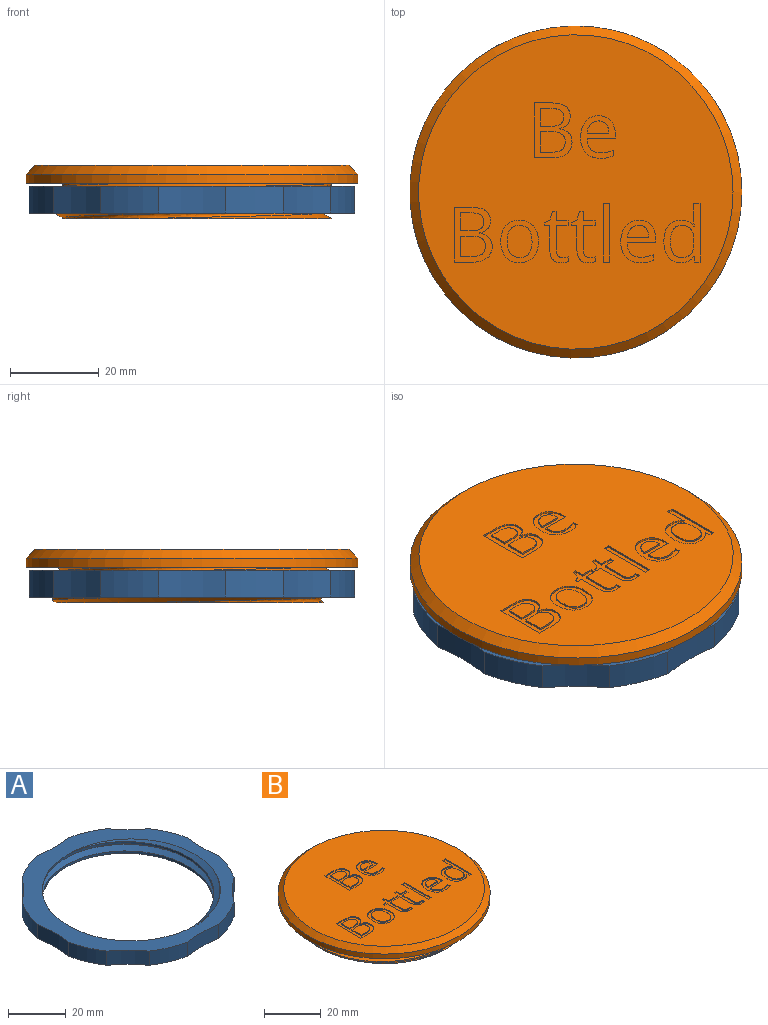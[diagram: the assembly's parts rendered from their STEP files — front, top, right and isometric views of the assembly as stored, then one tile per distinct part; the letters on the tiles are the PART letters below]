
ASSEMBLY  parts=2 mates=1
PART A: 22 faces, bbox 74.7x75.4x10.5 mm
  f0: plane 74.73x74.73mm, normal (0,0,-1), area 1345.5mm2, adj f1,f2,f3,f4,f5,f6,f7,f9
  f1: cylinder r=37.5mm len=13.18mm, axis (0,0,-1), area 86.1mm2, adj f0,f8,f14,f21
  f2: cylinder r=37.5mm len=13.18mm, axis (0,0,-1), area 86.1mm2, adj f0,f8,f20,f21
  f3: cylinder r=37.5mm len=13.18mm, axis (0,0,-1), area 86.1mm2, adj f0,f8,f19,f20
  f4: cylinder r=37.5mm len=13.18mm, axis (0,0,-1), area 86.1mm2, adj f0,f8,f18,f19
  f5: cylinder r=37.5mm len=13.18mm, axis (0,0,-1), area 86.1mm2, adj f0,f8,f17,f18
  f6: cylinder r=37.5mm len=13.18mm, axis (0,0,-1), area 86.1mm2, adj f0,f8,f16,f17
  f7: cylinder r=37.5mm len=13.18mm, axis (0,0,-1), area 86.1mm2, adj f0,f8,f15,f16
  f8: plane 74.73x74.73mm, normal (0,0,1), area 1345.4mm2, adj f1,f2,f3,f4,f5,f6,f7,f9
  f9: cylinder r=37.5mm len=13.18mm, axis (0,0,-1), area 86.1mm2, adj f0,f8,f14,f15
  f10: bspline ~73.7x63.83mm, area 726.9mm2, adj f0,f8,f12,f13
  f11: bspline ~73.7x63.83mm, area 726.7mm2, adj f0,f8,f12,f13
  f12: bspline ~74.12x64.19mm, area 174.8mm2, adj f0,f8,f10,f11
  f13: cylinder r=29.75mm len=59.5mm, axis (0,0,-1), area 280.5mm2, adj f0,f8,f10,f11
  f14: cylinder r=48.3mm len=10.61mm, axis (0,0,-1), area 90.4mm2, adj f0,f1,f8,f9
  f15: cylinder r=48.3mm len=15mm, axis (0,0,-1), area 90.4mm2, adj f0,f7,f8,f9
  f16: cylinder r=48.3mm len=10.61mm, axis (0,0,-1), area 90.4mm2, adj f0,f6,f7,f8
  f17: cylinder r=48.3mm len=15mm, axis (0,0,-1), area 90.4mm2, adj f0,f5,f6,f8
  f18: cylinder r=48.3mm len=10.61mm, axis (0,0,-1), area 90.4mm2, adj f0,f4,f5,f8
  f19: cylinder r=48.3mm len=15mm, axis (0,0,-1), area 90.4mm2, adj f0,f3,f4,f8
  f20: cylinder r=48.3mm len=10.61mm, axis (0,0,-1), area 90.4mm2, adj f0,f2,f3,f8
  f21: cylinder r=48.3mm len=15mm, axis (0,0,-1), area 90.4mm2, adj f0,f1,f2,f8
PART B: 197 faces, bbox 76.2x76.2x14.9 mm
  f0: plane 71x71mm, normal (0,0,1), area 3474.3mm2, adj f4,f9,f10,f11,f12,f13,f14,f15
  f1: plane 61.87x61.65mm, normal (0,0,-1), area 2876.1mm2, adj f5,f6,f7,f8
  f2: cylinder r=37.5mm len=75mm, axis (0,0,-1), area 471.2mm2, adj f3,f4
  f3: plane 76.2x76.2mm, normal (0,0,-1), area 1541.8mm2, adj f2,f5,f6,f7,f8
  f4: cone r=35.5mm half-angle=45deg, axis (0,0,-1), area 648.7mm2, adj f0,f2
  f5: cylinder r=31.5mm len=63mm, axis (0,0,1), area 197.8mm2, adj f1,f3,f7,f8
  f6: bspline ~67.75x58.67mm, area 411mm2, adj f1,f3,f7,f8
  f7: bspline ~72.75x63mm, area 955.9mm2, adj f1,f3,f5,f6
  f8: bspline ~72.75x63mm, area 955.9mm2, adj f1,f3,f5,f6
  f9: extruded ~0.72x0.4mm, area 0.3mm2, adj f0,f10,f27,f28
  f10: extruded ~1.09x0.45mm, area 0.5mm2, adj f0,f9,f11,f28
  f11: extruded ~1.29x0.4mm, area 0.6mm2, adj f0,f10,f12,f28
  f12: plane 5.46x0.4mm, normal (-1,0,0), area 2.2mm2, adj f0,f11,f13,f28
  f13: plane 2.69x0.4mm, normal (0,1,0), area 1.1mm2, adj f0,f12,f14,f28
  f14: plane 1.09x0.4mm, normal (-1,0,0), area 0.4mm2, adj f0,f13,f15,f28
  f15: plane 2.69x0.4mm, normal (0,-1,0), area 1.1mm2, adj f0,f14,f16,f28
  f16: plane 2.15x0.4mm, normal (-1,0,0), area 0.9mm2, adj f0,f15,f17,f28
  f17: plane 0.81x0.4mm, normal (0,-1,0), area 0.3mm2, adj f0,f16,f18,f28
  f18: plane 1.98x0.59mm, normal (0.96,-0.29,0), area 0.8mm2, adj f0,f17,f19,f28
  f19: plane 1.33x0.59mm, normal (0.4,-0.92,0), area 0.6mm2, adj f0,f18,f20,f28
  f20: plane 0.68x0.4mm, normal (1,0,0), area 0.3mm2, adj f0,f19,f21,f28
  f21: plane 1.33x0.4mm, normal (0,1,0), area 0.5mm2, adj f0,f20,f22,f28
  f22: plane 5.52x0.4mm, normal (1,0,0), area 2.2mm2, adj f0,f21,f23,f28
  f23: extruded ~2.84x2.69mm, area 1.8mm2, adj f0,f22,f24,f28
  f24: extruded ~0.8x0.4mm, area 0.3mm2, adj f0,f23,f25,f28
  f25: extruded ~0.67x0.4mm, area 0.3mm2, adj f0,f24,f26,f28
  f26: plane 1.08x0.4mm, normal (-1,0,0), area 0.4mm2, adj f0,f25,f27,f28
  f27: extruded ~0.55x0.4mm, area 0.2mm2, adj f0,f9,f26,f28
  f28: plane 11.6x5.49mm, normal (0,0,1), area 22.3mm2, adj f9,f10,f11,f12,f13,f14,f15,f16
  f29: plane 4.63x0.4mm, normal (-1,0,0), area 1.9mm2, adj f30,f53,f54,f191
  f30: plane 2.47x0.4mm, normal (0,1,0), area 1mm2, adj f29,f31,f54,f191
  f31: extruded ~2.36x0.54mm, area 1mm2, adj f30,f32,f54,f191
  f32: extruded ~1.69x0.78mm, area 0.8mm2, adj f31,f33,f54,f191
  f33: extruded ~1.82x0.76mm, area 0.8mm2, adj f32,f34,f54,f191
  f34: extruded ~2.26x0.58mm, area 0.9mm2, adj f33,f53,f54,f191
  f35: plane 2.37x0.4mm, normal (0,-1,0), area 0.9mm2, adj f36,f51,f54,f55
  f36: plane 4.05x0.4mm, normal (-1,0,0), area 1.6mm2, adj f35,f37,f54,f55
  f37: plane 2.12x0.4mm, normal (0,1,0), area 0.8mm2, adj f36,f38,f54,f55
  f38: extruded ~2.37x0.46mm, area 1mm2, adj f37,f39,f54,f55
  f39: extruded ~1.5x0.75mm, area 0.7mm2, adj f38,f40,f54,f55
  f40: extruded ~1.61x0.67mm, area 0.7mm2, adj f39,f51,f54,f55
  f41: plane 3.5x0.4mm, normal (0,-1,0), area 1.4mm2, adj f0,f42,f52,f54
  f42: plane 12.38x0.4mm, normal (1,0,0), area 5mm2, adj f0,f41,f43,f54
  f43: plane 4.32x0.4mm, normal (0,1,0), area 1.7mm2, adj f0,f42,f44,f54
  f44: extruded ~3.14x0.93mm, area 1.3mm2, adj f0,f43,f45,f54
  f45: extruded ~2.59x1.12mm, area 1.2mm2, adj f0,f44,f46,f54
  f46: extruded ~2.96x2.82mm, area 1.8mm2, adj f0,f45,f47,f54
  f47: plane 0.4x0.08mm, normal (-1,0,0), area 0mm2, adj f0,f46,f48,f54
  f48: extruded ~1.79x0.93mm, area 0.8mm2, adj f0,f47,f49,f54
  f49: extruded ~1.82x0.61mm, area 0.8mm2, adj f0,f48,f50,f54
  f50: extruded ~2.33x1.1mm, area 1.1mm2, adj f0,f49,f52,f54
  f51: extruded ~2.19x0.48mm, area 0.9mm2, adj f35,f40,f54,f55
  f52: extruded ~3.56x0.74mm, area 1.5mm2, adj f0,f41,f50,f54
  f53: plane 2.58x0.4mm, normal (0,-1,0), area 1mm2, adj f29,f34,f54,f191
  f54: plane 12.38x8.58mm, normal (0,0,1), area 52.3mm2, adj f29,f30,f31,f32,f33,f34,f35,f36
  f55: plane 5.23x4.05mm, normal (0,0,1), area 19.4mm2, adj f35,f36,f37,f38,f39,f40,f51
  f56: plane 4.63x0.4mm, normal (-1,0,0), area 1.9mm2, adj f57,f80,f81,f192
  f57: plane 2.47x0.4mm, normal (0,1,0), area 1mm2, adj f56,f58,f81,f192
  f58: extruded ~2.36x0.54mm, area 1mm2, adj f57,f59,f81,f192
  f59: extruded ~1.69x0.78mm, area 0.8mm2, adj f58,f60,f81,f192
  f60: extruded ~1.82x0.76mm, area 0.8mm2, adj f59,f61,f81,f192
  f61: extruded ~2.26x0.58mm, area 0.9mm2, adj f60,f80,f81,f192
  f62: plane 2.37x0.4mm, normal (0,-1,0), area 0.9mm2, adj f63,f78,f81,f82
  f63: plane 4.05x0.4mm, normal (-1,0,0), area 1.6mm2, adj f62,f64,f81,f82
  f64: plane 2.12x0.4mm, normal (0,1,0), area 0.8mm2, adj f63,f65,f81,f82
  f65: extruded ~2.37x0.46mm, area 1mm2, adj f64,f66,f81,f82
  f66: extruded ~1.5x0.75mm, area 0.7mm2, adj f65,f67,f81,f82
  f67: extruded ~1.61x0.67mm, area 0.7mm2, adj f66,f78,f81,f82
  f68: plane 3.5x0.4mm, normal (0,-1,0), area 1.4mm2, adj f0,f69,f79,f81
  f69: plane 12.38x0.4mm, normal (1,0,0), area 5mm2, adj f0,f68,f70,f81
  f70: plane 4.32x0.4mm, normal (0,1,0), area 1.7mm2, adj f0,f69,f71,f81
  f71: extruded ~3.14x0.93mm, area 1.3mm2, adj f0,f70,f72,f81
  f72: extruded ~2.59x1.12mm, area 1.2mm2, adj f0,f71,f73,f81
  f73: extruded ~2.96x2.82mm, area 1.8mm2, adj f0,f72,f74,f81
  f74: plane 0.4x0.08mm, normal (-1,0,0), area 0mm2, adj f0,f73,f75,f81
  f75: extruded ~1.79x0.93mm, area 0.8mm2, adj f0,f74,f76,f81
  f76: extruded ~1.82x0.61mm, area 0.8mm2, adj f0,f75,f77,f81
  f77: extruded ~2.33x1.1mm, area 1.1mm2, adj f0,f76,f79,f81
  f78: extruded ~2.19x0.48mm, area 0.9mm2, adj f62,f67,f81,f82
  f79: extruded ~3.56x0.74mm, area 1.5mm2, adj f0,f68,f77,f81
  f80: plane 2.58x0.4mm, normal (0,-1,0), area 1mm2, adj f56,f61,f81,f192
  f81: plane 12.38x8.58mm, normal (0,0,1), area 52.3mm2, adj f56,f57,f58,f59,f60,f61,f62,f63
  f82: plane 5.23x4.05mm, normal (0,0,1), area 19.4mm2, adj f62,f63,f64,f65,f66,f67,f78
  f83: extruded ~2.09x0.78mm, area 0.9mm2, adj f84,f106,f107,f193
  f84: extruded ~1.91x0.91mm, area 0.9mm2, adj f83,f85,f107,f193
  f85: extruded ~2.68x0.65mm, area 1.1mm2, adj f84,f86,f107,f193
  f86: extruded ~2.71x0.66mm, area 1.1mm2, adj f85,f87,f107,f193
  f87: extruded ~1.89x0.96mm, area 0.9mm2, adj f86,f88,f107,f193
  f88: extruded ~2.09x0.84mm, area 0.9mm2, adj f87,f89,f107,f193
  f89: extruded ~2.82x0.66mm, area 1.2mm2, adj f88,f90,f107,f193
  f90: plane 0.4x0.3mm, normal (1,0,0), area 0.1mm2, adj f89,f106,f107,f193
  f91: plane 0.4x0.08mm, normal (0,1,0), area 0mm2, adj f0,f92,f105,f107
  f92: plane 1.24x0.4mm, normal (0.99,0.15,0), area 0.5mm2, adj f0,f91,f93,f107
  f93: plane 1.14x0.4mm, normal (0,1,0), area 0.5mm2, adj f0,f92,f94,f107
  f94: plane 13.17x0.4mm, normal (-1,0,0), area 5.3mm2, adj f0,f93,f95,f107
  f95: plane 1.41x0.4mm, normal (0,-1,0), area 0.6mm2, adj f0,f94,f96,f107
  f96: plane 3.78x0.4mm, normal (1,0,0), area 1.5mm2, adj f0,f95,f97,f107
  f97: plane 0.65x0.4mm, normal (1,0.05,0), area 0.3mm2, adj f0,f96,f98,f107
  f98: plane 0.67x0.4mm, normal (1,0.09,0), area 0.3mm2, adj f0,f97,f99,f107
  f99: plane 0.4x0.11mm, normal (0,-1,0), area 0mm2, adj f0,f98,f100,f107
  f100: extruded ~2.9x1.37mm, area 1.3mm2, adj f0,f99,f101,f107
  f101: extruded ~2.83x1.27mm, area 1.3mm2, adj f0,f100,f102,f107
  f102: extruded ~3.57x1.02mm, area 1.5mm2, adj f0,f101,f103,f107
  f103: extruded ~3.54x1.01mm, area 1.5mm2, adj f0,f102,f104,f107
  f104: extruded ~2.83x1.25mm, area 1.3mm2, adj f0,f103,f105,f107
  f105: extruded ~2.91x1.41mm, area 1.4mm2, adj f0,f91,f104,f107
  f106: extruded ~2.53x0.65mm, area 1.1mm2, adj f83,f90,f107,f193
  f107: plane 13.35x8.16mm, normal (0,0,1), area 42mm2, adj f83,f84,f85,f86,f87,f88,f89,f90
  f108: extruded ~1.78x0.73mm, area 0.8mm2, adj f109,f126,f127,f194
  f109: extruded ~1.69x0.71mm, area 0.8mm2, adj f108,f110,f127,f194
  f110: extruded ~2.03x0.59mm, area 0.9mm2, adj f109,f111,f127,f194
  f111: plane 4.85x0.4mm, normal (0,-1,0), area 1.9mm2, adj f110,f126,f127,f194
  f112: extruded ~3.25x1.25mm, area 1.4mm2, adj f0,f113,f125,f127
  f113: extruded ~1.6x0.4mm, area 0.6mm2, adj f0,f112,f114,f127
  f114: extruded ~1.41x0.46mm, area 0.6mm2, adj f0,f113,f115,f127
  f115: plane 1.25x0.4mm, normal (-1,0,0), area 0.5mm2, adj f0,f114,f116,f127
  f116: extruded ~2.96x0.63mm, area 1.2mm2, adj f0,f115,f117,f127
  f117: extruded ~2.21x0.85mm, area 1mm2, adj f0,f116,f118,f127
  f118: extruded ~2.48x0.83mm, area 1.1mm2, adj f0,f117,f119,f127
  f119: plane 6.39x0.4mm, normal (0,1,0), area 2.6mm2, adj f0,f118,f120,f127
  f120: plane 0.89x0.4mm, normal (-1,0,0), area 0.4mm2, adj f0,f119,f121,f127
  f121: extruded ~3.03x1.02mm, area 1.3mm2, adj f0,f120,f122,f127
  f122: extruded ~2.76x1.15mm, area 1.2mm2, adj f0,f121,f123,f127
  f123: extruded ~2.97x1.32mm, area 1.3mm2, adj f0,f122,f124,f127
  f124: extruded ~3.57x1.11mm, area 1.5mm2, adj f0,f123,f125,f127
  f125: extruded ~3.48x1.19mm, area 1.5mm2, adj f0,f112,f124,f127
  f126: extruded ~2.01x0.78mm, area 0.9mm2, adj f108,f111,f127,f194
  f127: plane 9.62x7.85mm, normal (0,0,1), area 34.3mm2, adj f108,f109,f110,f111,f112,f113,f114,f115
  f128: extruded ~0.72x0.4mm, area 0.3mm2, adj f0,f129,f146,f147
  f129: extruded ~1.09x0.45mm, area 0.5mm2, adj f0,f128,f130,f147
  f130: extruded ~1.29x0.4mm, area 0.6mm2, adj f0,f129,f131,f147
  f131: plane 5.46x0.4mm, normal (-1,0,0), area 2.2mm2, adj f0,f130,f132,f147
  f132: plane 2.69x0.4mm, normal (0,1,0), area 1.1mm2, adj f0,f131,f133,f147
  f133: plane 1.09x0.4mm, normal (-1,0,0), area 0.4mm2, adj f0,f132,f134,f147
  f134: plane 2.69x0.4mm, normal (0,-1,0), area 1.1mm2, adj f0,f133,f135,f147
  f135: plane 2.15x0.4mm, normal (-1,0,0), area 0.9mm2, adj f0,f134,f136,f147
  f136: plane 0.81x0.4mm, normal (0,-1,0), area 0.3mm2, adj f0,f135,f137,f147
  f137: plane 1.98x0.59mm, normal (0.96,-0.29,0), area 0.8mm2, adj f0,f136,f138,f147
  f138: plane 1.33x0.59mm, normal (0.4,-0.92,0), area 0.6mm2, adj f0,f137,f139,f147
  f139: plane 0.68x0.4mm, normal (1,0,0), area 0.3mm2, adj f0,f138,f140,f147
  f140: plane 1.33x0.4mm, normal (0,1,0), area 0.5mm2, adj f0,f139,f141,f147
  f141: plane 5.52x0.4mm, normal (1,0,0), area 2.2mm2, adj f0,f140,f142,f147
  f142: extruded ~2.84x2.69mm, area 1.8mm2, adj f0,f141,f143,f147
  f143: extruded ~0.8x0.4mm, area 0.3mm2, adj f0,f142,f144,f147
  f144: extruded ~0.67x0.4mm, area 0.3mm2, adj f0,f143,f145,f147
  f145: plane 1.08x0.4mm, normal (-1,0,0), area 0.4mm2, adj f0,f144,f146,f147
  f146: extruded ~0.55x0.4mm, area 0.2mm2, adj f0,f128,f145,f147
  f147: plane 11.6x5.49mm, normal (0,0,1), area 22.3mm2, adj f128,f129,f130,f131,f132,f133,f134,f135
  f148: plane 1.41x0.4mm, normal (0,1,0), area 0.6mm2, adj f0,f149,f151,f152
  f149: plane 13.17x0.4mm, normal (-1,0,0), area 5.3mm2, adj f0,f148,f150,f152
  f150: plane 1.41x0.4mm, normal (0,-1,0), area 0.6mm2, adj f0,f149,f151,f152
  f151: plane 13.17x0.4mm, normal (1,0,0), area 5.3mm2, adj f0,f148,f150,f152
  f152: plane 13.17x1.41mm, normal (0,0,1), area 18.5mm2, adj f148,f149,f150,f151
  f153: extruded ~1.78x0.73mm, area 0.8mm2, adj f154,f171,f172,f195
  f154: extruded ~1.69x0.71mm, area 0.8mm2, adj f153,f155,f172,f195
  f155: extruded ~2.03x0.59mm, area 0.9mm2, adj f154,f156,f172,f195
  f156: plane 4.85x0.4mm, normal (0,-1,0), area 1.9mm2, adj f155,f171,f172,f195
  f157: extruded ~3.25x1.25mm, area 1.4mm2, adj f0,f158,f170,f172
  f158: extruded ~1.6x0.4mm, area 0.6mm2, adj f0,f157,f159,f172
  f159: extruded ~1.41x0.46mm, area 0.6mm2, adj f0,f158,f160,f172
  f160: plane 1.25x0.4mm, normal (-1,0,0), area 0.5mm2, adj f0,f159,f161,f172
  f161: extruded ~2.96x0.63mm, area 1.2mm2, adj f0,f160,f162,f172
  f162: extruded ~2.21x0.85mm, area 1mm2, adj f0,f161,f163,f172
  f163: extruded ~2.48x0.83mm, area 1.1mm2, adj f0,f162,f164,f172
  f164: plane 6.39x0.4mm, normal (0,1,0), area 2.6mm2, adj f0,f163,f165,f172
  f165: plane 0.89x0.4mm, normal (-1,0,0), area 0.4mm2, adj f0,f164,f166,f172
  f166: extruded ~3.03x1.02mm, area 1.3mm2, adj f0,f165,f167,f172
  f167: extruded ~2.76x1.15mm, area 1.2mm2, adj f0,f166,f168,f172
  f168: extruded ~2.97x1.32mm, area 1.3mm2, adj f0,f167,f169,f172
  f169: extruded ~3.57x1.11mm, area 1.5mm2, adj f0,f168,f170,f172
  f170: extruded ~3.48x1.19mm, area 1.5mm2, adj f0,f157,f169,f172
  f171: extruded ~2.01x0.78mm, area 0.9mm2, adj f153,f156,f172,f195
  f172: plane 9.62x7.85mm, normal (0,0,1), area 34.3mm2, adj f153,f154,f155,f156,f157,f158,f159,f160
  f173: extruded ~2.71x0.71mm, area 1.1mm2, adj f174,f189,f190,f196
  f174: extruded ~2.7x0.7mm, area 1.1mm2, adj f173,f175,f190,f196
  f175: extruded ~2.08x0.91mm, area 0.9mm2, adj f174,f176,f190,f196
  f176: extruded ~2.11x0.92mm, area 1mm2, adj f175,f177,f190,f196
  f177: extruded ~2.69x0.72mm, area 1.1mm2, adj f176,f178,f190,f196
  f178: extruded ~2.71x0.72mm, area 1.1mm2, adj f177,f179,f190,f196
  f179: extruded ~2.1x0.93mm, area 1mm2, adj f178,f189,f190,f196
  f180: extruded ~3.55x1.14mm, area 1.5mm2, adj f0,f181,f188,f190
  f181: extruded ~3.5x1.15mm, area 1.5mm2, adj f0,f180,f182,f190
  f182: extruded ~3.09x1.3mm, area 1.4mm2, adj f0,f181,f183,f190
  f183: extruded ~3.15x1.27mm, area 1.4mm2, adj f0,f182,f184,f190
  f184: extruded ~3.53x1.14mm, area 1.5mm2, adj f0,f183,f185,f190
  f185: extruded ~2.56x0.53mm, area 1.1mm2, adj f0,f184,f186,f190
  f186: extruded ~1.68x1.49mm, area 0.9mm2, adj f0,f185,f187,f190
  f187: extruded ~2.21x0.59mm, area 0.9mm2, adj f0,f186,f188,f190
  f188: extruded ~3.16x1.27mm, area 1.4mm2, adj f0,f180,f187,f190
  f189: extruded ~2.09x0.93mm, area 1mm2, adj f173,f179,f190,f196
  f190: plane 9.62x8.53mm, normal (0,0,1), area 33.1mm2, adj f173,f174,f175,f176,f177,f178,f179,f180
  f191: plane 5.6x4.63mm, normal (0,0,1), area 23.6mm2, adj f29,f30,f31,f32,f33,f34,f53
  f192: plane 5.6x4.63mm, normal (0,0,1), area 23.6mm2, adj f56,f57,f58,f59,f60,f61,f80
  f193: plane 7.26x5.3mm, normal (0,0,1), area 32.4mm2, adj f83,f84,f85,f86,f87,f88,f89,f90
  f194: plane 4.85x2.74mm, normal (0,0,1), area 10.7mm2, adj f108,f109,f110,f111,f126
  f195: plane 4.85x2.74mm, normal (0,0,1), area 10.7mm2, adj f153,f154,f155,f156,f171
  f196: plane 7.25x5.61mm, normal (0,0,1), area 33.7mm2, adj f173,f174,f175,f176,f177,f178,f179,f189
PLACE A t=(0,0,-14.25)mm
PLACE B t=(0,0,-7.5)mm
MATE cylindrical B.f5 <-> A.f1  axis (0,0,-1) through (0,0,-15.5)mm
